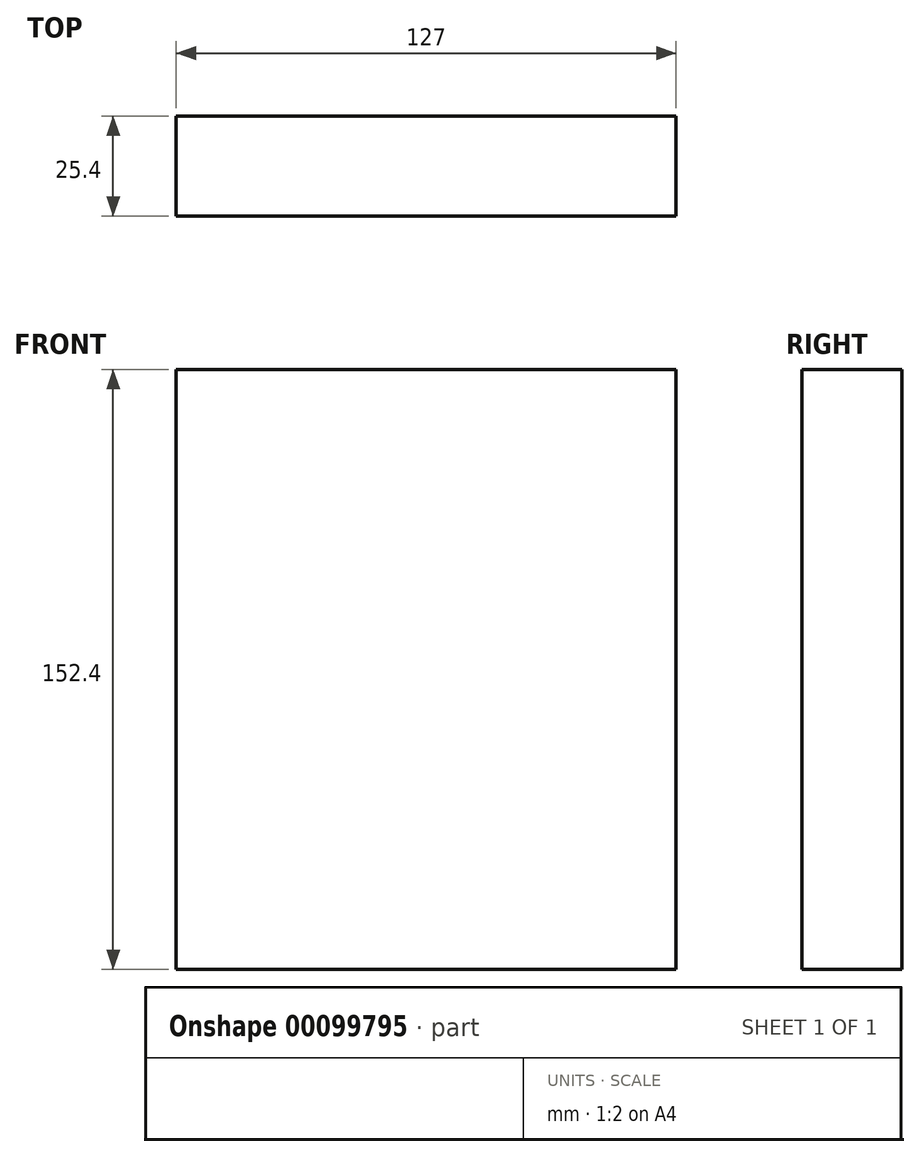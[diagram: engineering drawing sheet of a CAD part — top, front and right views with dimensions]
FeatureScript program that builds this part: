
annotation { "Feature Type Name" : "Feature", "Feature Type Description" : "" }
export const myFeature = defineFeature(function(context is Context, id is Id, definition is map)
    precondition{}
    {
        {
            var Q0;
            Q0=qCreatedBy(makeId("Front.planeOp"),FACE);
            var sketch = newSketch(context, id + "F0", { "sketchPlane" : qUnion([Q0])});
            skLineSegment(sketch, "E0.bottom", {"start": v(-67.02, 91.83) * mm, "end": v(59.98, 91.83) * mm});
            skLineSegment(sketch, "E0.top", {"start": v(-67.02, -60.57) * mm, "end": v(59.98, -60.57) * mm});
            skLineSegment(sketch, "E0.left", {"start": v(-67.02, 91.83) * mm, "end": v(-67.02, -60.57) * mm});
            skLineSegment(sketch, "E0.right", {"start": v(59.98, 91.83) * mm, "end": v(59.98, -60.57) * mm});
            skSolve(sketch);
        }
        {
            var Q0;
            Q0=makeQuery(id+"F0.imprint","IMPRINT",FACE,{"disambiguationData":[TD([[makeQuery(id+"F0.imprint","IMPRINT",EDGE,{"derivedFrom":sQuery(id+"F0.wireOp",EDGE,"E0.bottom")}),-1.0]])]});
            extrude(context, id + "F1", {"entities" : qUnion([Q0]), "depth" : 25.4 * mm});
        }
    });
